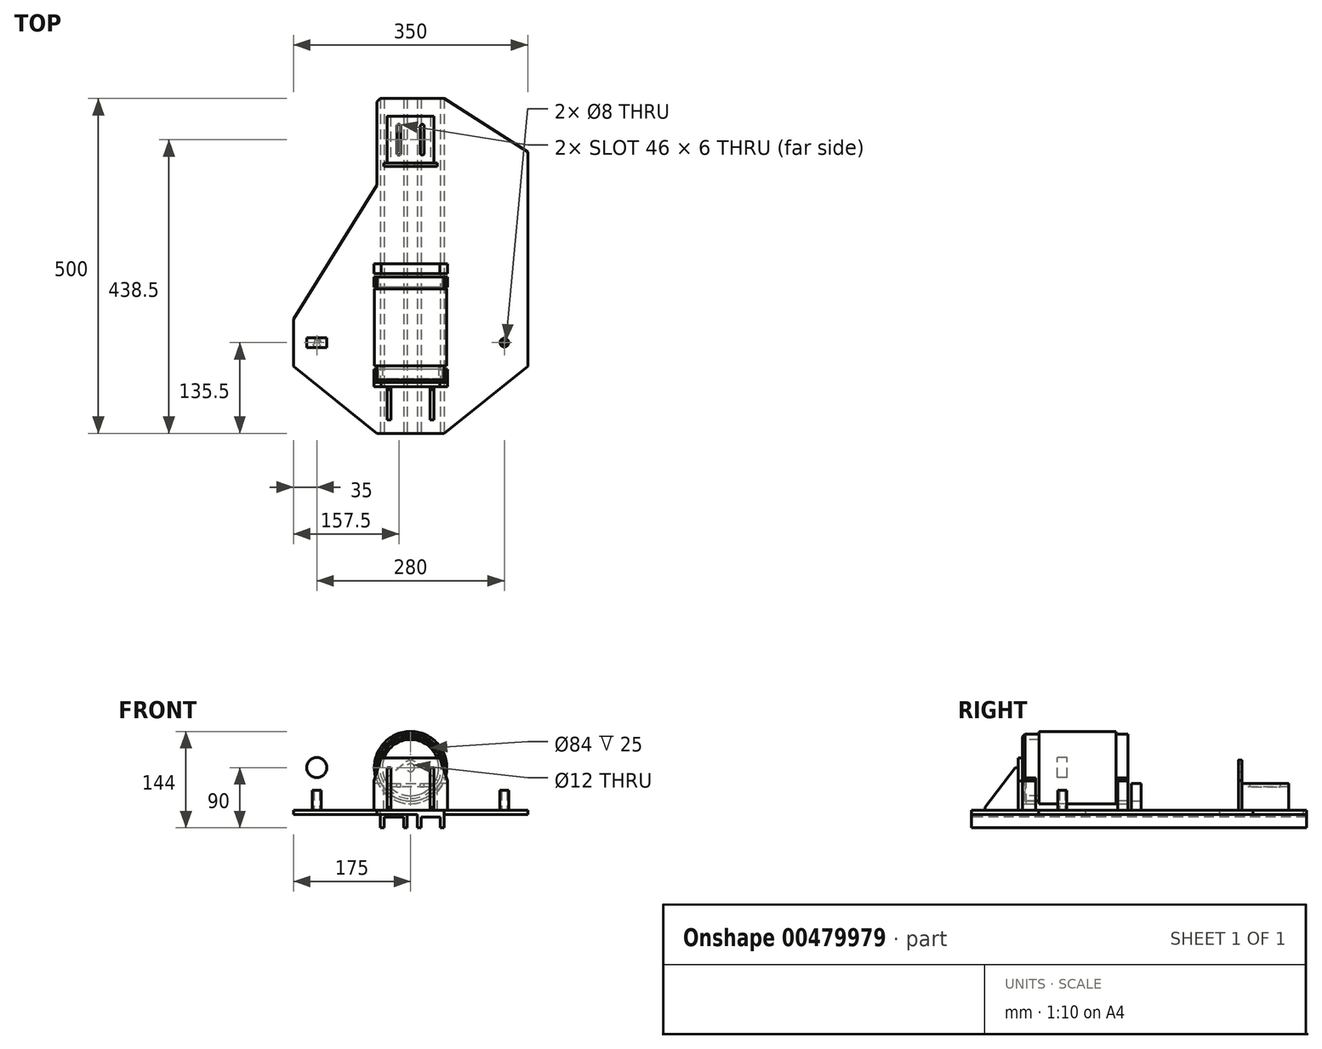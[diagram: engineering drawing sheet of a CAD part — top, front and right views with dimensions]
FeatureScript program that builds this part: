
annotation { "Feature Type Name" : "Feature", "Feature Type Description" : "" }
export const myFeature = defineFeature(function(context is Context, id is Id, definition is map)
    precondition{}
    {
        {
            var Q0;
            Q0=qCreatedBy(makeId("Front.planeOp"),FACE);
            var sketch = newSketch(context, id + "F0", { "sketchPlane" : qUnion([Q0])});
            skCircle(sketch, "E0", {"center": v(0, 0) * mm, "radius": 50 * mm});
            skSolve(sketch);
        }
        {
            var Q0;
            Q0=makeQuery(id+"F0.imprint","IMPRINT",FACE,{"disambiguationData":[TD([[makeQuery(id+"F0.imprint","IMPRINT",EDGE,{"derivedFrom":sQuery(id+"F0.wireOp",EDGE,"E0")}),1.0]])]});
            extrude(context, id + "F1", {"entities" : qUnion([Q0]), "oppositeDirection" : true, "depth" : 25 * mm});
        }
        {
            var Q0;
            Q0=makeQuery(id+"F1.opExtrude","CAP_FACE",FACE,{"disambiguationData":[OSD([sQuery(id+"F0.wireOp",EDGE,"E0")])],"isStart":false});
            var sketch = newSketch(context, id + "F2", { "sketchPlane" : qUnion([Q0])});
            skCircle(sketch, "E1", {"center": v(0, 0) * mm, "radius": 54 * mm});
            skSolve(sketch);
        }
        {
            var Q0;
            Q0=makeQuery(id+"F2.imprint","IMPRINT",FACE,{"disambiguationData":[TD([[makeQuery(id+"F2.imprint","IMPRINT",EDGE,{"derivedFrom":sQuery(id+"F2.wireOp",EDGE,"E1")}),1.0]])]});
            var Q1;
            Q1=makeQuery(id+"F2.imprint","IMPRINT",FACE,{"disambiguationData":[TD([[makeQuery(id+"F2.imprint","IMPRINT",EDGE,{"derivedFrom":makeQuery(id+"F1.opExtrude","CAP_EDGE",EDGE,{"disambiguationData":[OSD([sQuery(id+"F0.wireOp",EDGE,"E0")])],"isStart":false})}),-1.0]])]});
            extrude(context, id + "F3", {"entities" : qUnion([Q0, Q1]), "operationType" : NewBodyOperationType.ADD, "depth" : 115 * mm});
        }
        {
            var Q0;
            Q0=makeQuery(id+"F3.opExtrude","CAP_FACE",FACE,{"disambiguationData":[OSD([sQuery(id+"F2.wireOp",EDGE,"E1")])],"isStart":false});
            var sketch = newSketch(context, id + "F4", { "sketchPlane" : qUnion([Q0])});
            skCircle(sketch, "E2", {"center": v(0, 0) * mm, "radius": 50 * mm});
            skSolve(sketch);
        }
        {
            var Q0;
            Q0=makeQuery(id+"F4.imprint","IMPRINT",FACE,{"disambiguationData":[TD([[makeQuery(id+"F4.imprint","IMPRINT",EDGE,{"derivedFrom":sQuery(id+"F4.wireOp",EDGE,"E2")}),1.0]])]});
            extrude(context, id + "F5", {"entities" : qUnion([Q0]), "operationType" : NewBodyOperationType.ADD, "depth" : 17.5 * mm});
        }
        {
            var Q0;
            Q0=makeQuery(id+"F0.imprint","IMPRINT",FACE,{"disambiguationData":[TD([[makeQuery(id+"F0.imprint","IMPRINT",EDGE,{"derivedFrom":sQuery(id+"F0.wireOp",EDGE,"E0")}),1.0]])]});
            var sketch = newSketch(context, id + "F6", { "sketchPlane" : qUnion([Q0])});
            skCircle(sketch, "E3", {"center": v(0, 0) * mm, "radius": 42 * mm});
            skSolve(sketch);
        }
        {
            var Q0;
            Q0=makeQuery(id+"F6.imprint","IMPRINT",FACE,{"disambiguationData":[TD([[makeQuery(id+"F6.imprint","IMPRINT",EDGE,{"derivedFrom":sQuery(id+"F6.wireOp",EDGE,"E3")}),1.0]])]});
            var Q1;
            Q1=sQuery(id+"F6.wireOp",EDGE,"E3");
            extrude(context, id + "F7", {"entities" : qUnion([Q0]), "operationType" : NewBodyOperationType.REMOVE, "surfaceEntities" : qUnion([Q1]), "oppositeDirection" : true, "depth" : 25 * mm, "offsetDistance" : 25 * mm});
        }
        {
            var Q0;
            Q0=makeQuery(id+"F3.opExtrude","CAP_FACE",FACE,{"disambiguationData":[OSD([sQuery(id+"F2.wireOp",EDGE,"E1")])],"isStart":true});
            cPlane(context, id + "F8", {"entities" : qUnion([Q0]), "cplaneType" : CPlaneType.OFFSET, "offset" : 27 * mm, "oppositeDirection" : true, "width" : 150 * mm, "height" : 150 * mm});
        }
        {
            var Q0;
            Q0=qCreatedBy(id+"F8.planeOp",FACE);
            var sketch = newSketch(context, id + "F9", { "sketchPlane" : qUnion([Q0])});
            skLineSegment(sketch, "E4", {"start": v(0, 0) * mm, "end": v(-140, 0) * mm, "construction": true});
            skCircle(sketch, "E5", {"center": v(-140, 0) * mm, "radius": 13.5 * mm});
            skCircle(sketch, "E6", {"center": v(-140, 0) * mm, "radius": 15 * mm});
            skSolve(sketch);
        }
        {
            var Q0;
            Q0=makeQuery(id+"F9.imprint","IMPRINT",FACE,{"disambiguationData":[TD([[makeQuery(id+"F9.imprint","IMPRINT",EDGE,{"derivedFrom":sQuery(id+"F9.wireOp",EDGE,"E5")}),1.0]])]});
            var Q1;
            Q1=makeQuery(id+"F9.imprint","IMPRINT",FACE,{"disambiguationData":[TD([[makeQuery(id+"F9.imprint","IMPRINT",EDGE,{"derivedFrom":sQuery(id+"F9.wireOp",EDGE,"E5")}),-1.0]])]});
            extrude(context, id + "F10", {"entities" : qUnion([Q0, Q1]), "oppositeDirection" : true, "depth" : 15 * mm});
        }
        {
            var Q0;
            Q0=makeQuery(id+"F5.opExtrude","CAP_FACE",FACE,{"disambiguationData":[OSD([sQuery(id+"F4.wireOp",EDGE,"E2")])],"isStart":false});
            var sketch = newSketch(context, id + "F11", { "sketchPlane" : qUnion([Q0])});
            skCircle(sketch, "E7.0", {"center": v(0, 0) * mm, "radius": 50 * mm});
            skLineSegment(sketch, "E8", {"start": v(0, 0) * mm, "end": v(-48.3, -12.94) * mm, "construction": true});
            skLineSegment(sketch, "E9", {"start": v(0, 0) * mm, "end": v(-50, 0) * mm, "construction": true});
            skLineSegment(sketch, "E10", {"start": v(-55, -19.64) * mm, "end": v(-55, -64) * mm});
            skLineSegment(sketch, "E11", {"start": v(-55, -64) * mm, "end": v(0, -64) * mm});
            skCircle(sketch, "E12.0", {"center": v(0, 0) * mm, "radius": 54 * mm});
            skLineSegment(sketch, "E13", {"start": v(-52.4, -15.69) * mm, "end": v(-47.48, -15.69) * mm});
            skLineSegment(sketch, "E14", {"start": v(0, -64) * mm, "end": v(55, -64) * mm});
            skLineSegment(sketch, "E15", {"start": v(55, -64) * mm, "end": v(55, -19.64) * mm});
            skLineSegment(sketch, "E16", {"start": v(0, 0) * mm, "end": v(0, -64) * mm, "construction": true});
            skLineSegment(sketch, "E17", {"start": v(52.4, -15.69) * mm, "end": v(47.48, -15.69) * mm});
            skLineSegment(sketch, "E18", {"start": v(-55, -19.64) * mm, "end": v(-52.4, -15.69) * mm});
            skLineSegment(sketch, "E19", {"start": v(55, -19.64) * mm, "end": v(52.4, -15.69) * mm});
            skLineSegment(sketch, "E20", {"start": v(0, 0) * mm, "end": v(-38.18, -38.18) * mm, "construction": true});
            skLineSegment(sketch, "E21", {"start": v(-35.36, -35.36) * mm, "end": v(0, -35.36) * mm, "construction": true});
            skSolve(sketch);
        }
        {
            var Q0;
            {var subQ0=sQuery(id+"F11.wireOp",EDGE,"E13");var subQ1=sQuery(id+"F11.wireOp",EDGE,"E7.0");var subQ2=makeQuery(id+"F11.imprint","INTERSECT",VERTEX,{"derivedFrom":[subQ1,subQ0]});Q0=makeQuery(id+"F11.imprint","IMPRINT",FACE,{"disambiguationData":[TD([[makeQuery(id+"F11.imprint","IMPRINT",EDGE,{"disambiguationData":[TD([[subQ2,-1.0]])],"derivedFrom":subQ1}),-1.0]])]});}
            extrude(context, id + "F12", {"entities" : qUnion([Q0]), "oppositeDirection" : true, "depth" : 15 * mm});
        }
        {
            var Q0;
            Q0=makeQuery(id+"F11.imprint","IMPRINT",FACE,{"disambiguationData":[TD([[makeQuery(id+"F11.imprint","IMPRINT",EDGE,{"derivedFrom":sQuery(id+"F11.wireOp",EDGE,"E10")}),1.0]])]});
            extrude(context, id + "F13", {"entities" : qUnion([Q0]), "oppositeDirection" : true, "depth" : 15 * mm});
        }
        {
            var Q0;
            Q0=makeQuery(id+"F12.opExtrude","SWEPT_BODY",BODY,{"disambiguationData":[OSD([sQuery(id+"F11.wireOp",EDGE,"E7.0"),sQuery(id+"F11.wireOp",EDGE,"E12.0"),sQuery(id+"F11.wireOp",EDGE,"E13"),sQuery(id+"F11.wireOp",EDGE,"E17")])]});
            transform(context, id + "F14", {"entities" : qUnion([Q0]), "transformType" : TransformType.TRANSLATION_3D, "dx" : 0 * mm, "dy" : -137.5 * mm, "dz" : 0 * mm, "makeCopy" : true});
        }
        {
            var Q0;
            Q0=makeQuery(id+"F1.opExtrude","CAP_FACE",FACE,{"disambiguationData":[OSD([sQuery(id+"F0.wireOp",EDGE,"E0")])],"isStart":true});
            var sketch = newSketch(context, id + "F15", { "sketchPlane" : qUnion([Q0])});
            skLineSegment(sketch, "E22.0", {"start": v(-55, -64) * mm, "end": v(-55, -19.64) * mm});
            skLineSegment(sketch, "E23.0", {"start": v(-55, -19.64) * mm, "end": v(-52.4, -15.69) * mm});
            skLineSegment(sketch, "E24.0", {"start": v(-52.4, -15.69) * mm, "end": v(-47.48, -15.69) * mm});
            skLineSegment(sketch, "E25.0", {"start": v(52.4, -15.69) * mm, "end": v(47.48, -15.69) * mm});
            skLineSegment(sketch, "E26.0", {"start": v(55, -19.64) * mm, "end": v(52.4, -15.69) * mm});
            skLineSegment(sketch, "E27.0", {"start": v(55, -19.64) * mm, "end": v(55, -64) * mm});
            skLineSegment(sketch, "E28.0", {"start": v(55, -64) * mm, "end": v(0, -64) * mm});
            skLineSegment(sketch, "E28.1", {"start": v(0, -64) * mm, "end": v(-55, -64) * mm});
            skArc(sketch, "E29.0", {"start": v(51.67, -15.69) * mm, "mid": v(0, -54) * mm, "end": v(-51.67, -15.69) * mm});
            skLineSegment(sketch, "E30", {"start": v(-52.4, -15.69) * mm, "end": v(-30, 18.29) * mm});
            skLineSegment(sketch, "E31", {"start": v(-30, 18.29) * mm, "end": v(0, 18.29) * mm});
            skLineSegment(sketch, "E32", {"start": v(0, 18.29) * mm, "end": v(30, 18.29) * mm});
            skLineSegment(sketch, "E33", {"start": v(30, 18.29) * mm, "end": v(52.4, -15.69) * mm});
            skLineSegment(sketch, "E34", {"start": v(0, 18.29) * mm, "end": v(0, -64) * mm, "construction": true});
            skSolve(sketch);
        }
        {
            var Q0;
            Q0=makeQuery(id+"F3.opExtrude","CAP_FACE",FACE,{"disambiguationData":[OSD([sQuery(id+"F2.wireOp",EDGE,"E1")])],"isStart":true});
            var sketch = newSketch(context, id + "F16", { "sketchPlane" : qUnion([Q0])});
            skLineSegment(sketch, "E35.0", {"start": v(-55, -64) * mm, "end": v(-55, -19.64) * mm});
            skLineSegment(sketch, "E35.1", {"start": v(0, -64) * mm, "end": v(-55, -64) * mm});
            skLineSegment(sketch, "E35.2", {"start": v(55, -19.64) * mm, "end": v(55, -64) * mm});
            skLineSegment(sketch, "E35.3", {"start": v(55, -64) * mm, "end": v(0, -64) * mm});
            skLineSegment(sketch, "E35.4", {"start": v(55, -19.64) * mm, "end": v(52.4, -15.69) * mm});
            skLineSegment(sketch, "E35.5", {"start": v(30, 18.29) * mm, "end": v(55, -19.64) * mm});
            skLineSegment(sketch, "E35.6", {"start": v(-55, -19.64) * mm, "end": v(-52.4, -15.69) * mm});
            skLineSegment(sketch, "E35.7", {"start": v(-55, -19.64) * mm, "end": v(-30, 18.29) * mm});
            skArc(sketch, "E36.0", {"start": v(51.67, -15.69) * mm, "mid": v(0, -54) * mm, "end": v(-51.67, -15.69) * mm});
            skLineSegment(sketch, "E37", {"start": v(-51.67, -15.69) * mm, "end": v(-52.4, -15.69) * mm});
            skLineSegment(sketch, "E38", {"start": v(51.67, -15.69) * mm, "end": v(52.4, -15.69) * mm});
            skSolve(sketch);
        }
        {
            var Q0;
            {var subQ2=sQuery(id+"F16.wireOp",EDGE,"E35.0");Q0=makeQuery(id+"F16.imprint","IMPRINT",FACE,{"disambiguationData":[TD([[makeQuery(id+"F16.imprint","IMPRINT",EDGE,{"derivedFrom":subQ2}),-1.0]])]});}
            extrude(context, id + "F17", {"entities" : qUnion([Q0]), "depth" : 25 * mm, "hasSecondDirection" : true, "secondDirectionOppositeDirection" : false, "secondDirectionDepth" : 5 * mm, "offsetDistance" : 25 * mm});
        }
        {
            var Q0;
            Q0=qCreatedBy(makeId("Right.planeOp"),FACE);
            cPlane(context, id + "F18", {"entities" : qUnion([Q0]), "cplaneType" : CPlaneType.OFFSET, "offset" : 35 * mm, "width" : 150 * mm, "height" : 150 * mm});
        }
        {
            var Q0;
            Q0=qCreatedBy(id+"F18.planeOp",FACE);
            var sketch = newSketch(context, id + "F19", { "sketchPlane" : qUnion([Q0])});
            skLineSegment(sketch, "E39.0", {"start": v(-6, 18.29) * mm, "end": v(-6, -19.64) * mm});
            skLineSegment(sketch, "E40.0", {"start": v(-6, -19.64) * mm, "end": v(-6, -64) * mm});
            skLineSegment(sketch, "E41", {"start": v(-6, -64) * mm, "end": v(-56, -64) * mm});
            skLineSegment(sketch, "E42", {"start": v(-56, -64) * mm, "end": v(-56, -59) * mm});
            skLineSegment(sketch, "E43", {"start": v(-56, -59) * mm, "end": v(-11, 0) * mm});
            skLineSegment(sketch, "E44", {"start": v(-11, 0) * mm, "end": v(-6, 0) * mm});
            skSolve(sketch);
        }
        {
            var Q0;
            {var subQ0=sQuery(id+"F19.wireOp",EDGE,"E40.0");Q0=makeQuery(id+"F19.imprint","IMPRINT",FACE,{"disambiguationData":[TD([[makeQuery(id+"F19.imprint","IMPRINT",EDGE,{"derivedFrom":subQ0}),-1.0]])]});}
            extrude(context, id + "F20", {"entities" : qUnion([Q0]), "oppositeDirection" : true, "depth" : 6 * mm});
        }
        {
            var Q0;
            Q0=makeQuery(id+"F20.opExtrude","SWEPT_BODY",BODY,{"disambiguationData":[OSD([sQuery(id+"F19.wireOp",EDGE,"E39.0"),sQuery(id+"F19.wireOp",EDGE,"E40.0"),sQuery(id+"F19.wireOp",EDGE,"E41"),sQuery(id+"F19.wireOp",EDGE,"E42"),sQuery(id+"F19.wireOp",EDGE,"E43"),sQuery(id+"F19.wireOp",EDGE,"E44")])]});
            transform(context, id + "F21", {"entities" : qUnion([Q0]), "transformType" : TransformType.TRANSLATION_3D, "dx" : -64 * mm, "dy" : 0 * mm, "dz" : 0 * mm, "makeCopy" : true});
        }
        {
            var Q0;
            {var subQ0=sQuery(id+"F11.wireOp",EDGE,"E7.0");var subQ1=makeQuery(id+"F11.imprint","INTERSECT",VERTEX,{"derivedFrom":[subQ0,sQuery(id+"F11.wireOp",EDGE,"E13")]});Q0=makeQuery(id+"F11.imprint","IMPRINT",FACE,{"disambiguationData":[TD([[makeQuery(id+"F11.imprint","IMPRINT",EDGE,{"disambiguationData":[TD([[subQ1,-1.0]])],"derivedFrom":subQ0}),1.0]])]});}
            cPlane(context, id + "F22", {"entities" : qUnion([Q0]), "cplaneType" : CPlaneType.OFFSET, "offset" : 25 * mm, "width" : 150 * mm, "height" : 150 * mm});
        }
        {
            var Q0;
            Q0=qCreatedBy(id+"F22.planeOp",FACE);
            var sketch = newSketch(context, id + "F23", { "sketchPlane" : qUnion([Q0])});
            skCircle(sketch, "E45.0", {"center": v(0, 0) * mm, "radius": 50 * mm});
            skLineSegment(sketch, "E46.0", {"start": v(0, -64) * mm, "end": v(55, -64) * mm});
            skLineSegment(sketch, "E46.1", {"start": v(-55, -64) * mm, "end": v(0, -64) * mm});
            skLineSegment(sketch, "E46.3", {"start": v(-55, -19.64) * mm, "end": v(-55, -64) * mm});
            skLineSegment(sketch, "E47", {"start": v(-55, -24) * mm, "end": v(-43.86, -24) * mm});
            skLineSegment(sketch, "E48", {"start": v(55, -64) * mm, "end": v(55, -19.64) * mm});
            skLineSegment(sketch, "E49", {"start": v(43.86, -24) * mm, "end": v(55, -24) * mm});
            skLineSegment(sketch, "E50", {"start": v(0, -64) * mm, "end": v(0, -22.33) * mm, "construction": true});
            skSolve(sketch);
        }
        {
            var Q0;
            Q0=makeQuery(id+"F23.imprint","IMPRINT",FACE,{"disambiguationData":[TD([[makeQuery(id+"F23.imprint","IMPRINT",EDGE,{"derivedFrom":sQuery(id+"F23.wireOp",EDGE,"E46.0")}),1.0]])]});
            extrude(context, id + "F24", {"entities" : qUnion([Q0]), "oppositeDirection" : true, "depth" : 20 * mm});
        }
        {
            var Q0;
            Q0=makeQuery(id+"F17.opExtrude","SWEPT_FACE",FACE,{"disambiguationData":[OSD([sQuery(id+"F16.wireOp",EDGE,"E35.1"),sQuery(id+"F16.wireOp",EDGE,"E35.3")])]});
            var sketch = newSketch(context, id + "F25", { "sketchPlane" : qUnion([Q0])});
            skLineSegment(sketch, "E51", {"start": v(-175, -24) * mm, "end": v(-175, -95) * mm});
            skLineSegment(sketch, "E52", {"start": v(-175, -95) * mm, "end": v(-50, -295) * mm});
            skLineSegment(sketch, "E53", {"start": v(-50, -295) * mm, "end": v(-50, -424) * mm});
            skLineSegment(sketch, "E54", {"start": v(-50, -424) * mm, "end": v(50, -424) * mm});
            skLineSegment(sketch, "E55", {"start": v(50, -424) * mm, "end": v(50, -295) * mm});
            skLineSegment(sketch, "E56", {"start": v(50, -295) * mm, "end": v(175, -95) * mm});
            skLineSegment(sketch, "E57", {"start": v(175, -95) * mm, "end": v(175, -24) * mm});
            skLineSegment(sketch, "E58", {"start": v(175, -24) * mm, "end": v(50, 76) * mm});
            skLineSegment(sketch, "E59", {"start": v(50, 76) * mm, "end": v(-50, 76) * mm});
            skLineSegment(sketch, "E60", {"start": v(-50, 76) * mm, "end": v(-175, -24) * mm});
            skLineSegment(sketch, "E61", {"start": v(0, 0) * mm, "end": v(0, -424) * mm, "construction": true});
            skLineSegment(sketch, "E62", {"start": v(-175, -59.5) * mm, "end": v(175, -59.5) * mm, "construction": true});
            skLineSegment(sketch, "E63.0", {"start": v(-155, -52) * mm, "end": v(-125, -52) * mm, "construction": true});
            skLineSegment(sketch, "E63.1", {"start": v(-155, -67) * mm, "end": v(-125, -67) * mm, "construction": true});
            skLineSegment(sketch, "E64", {"start": v(-155, -52) * mm, "end": v(-155, -67) * mm, "construction": true});
            skLineSegment(sketch, "E65", {"start": v(-155, -59.5) * mm, "end": v(-171.28, -59.5) * mm, "construction": true});
            skSolve(sketch);
        }
        {
            var Q0;
            Q0=makeQuery(id+"F25.imprint","IMPRINT",FACE,{"disambiguationData":[TD([[makeQuery(id+"F25.imprint","IMPRINT",EDGE,{"derivedFrom":sQuery(id+"F25.wireOp",EDGE,"E51")}),1.0]])]});
            var Q1;
            {var subQ0=sQuery(id+"F16.wireOp",EDGE,"E35.1");Q1=makeQuery(id+"F25.imprint","IMPRINT",FACE,{"disambiguationData":[TD([[makeQuery(id+"F25.imprint","IMPRINT",EDGE,{"derivedFrom":makeQuery(id+"F17.opExtrude","SWEPT_EDGE",EDGE,{"disambiguationData":[OSD([sQuery(id+"F16.wireOp",EDGE,"E35.0"),subQ0])]})}),1.0]])]});}
            extrude(context, id + "F26", {"entities" : qUnion([Q0, Q1]), "depth" : 6 * mm});
        }
        {
            var Q0;
            Q0=makeQuery(id+"F10.opExtrude","CAP_FACE",FACE,{"disambiguationData":[OSD([sQuery(id+"F9.wireOp",EDGE,"E6")])],"isStart":false});
            cPlane(context, id + "F27", {"entities" : qUnion([Q0]), "cplaneType" : CPlaneType.OFFSET, "offset" : 7.5 * mm, "oppositeDirection" : true, "width" : 150 * mm, "height" : 150 * mm});
        }
        {
            var Q0;
            Q0=qCreatedBy(id+"F27.planeOp",FACE);
            var sketch = newSketch(context, id + "F28", { "sketchPlane" : qUnion([Q0])});
            skCircle(sketch, "E66.0", {"center": v(140, 0) * mm, "radius": 15 * mm, "construction": true});
            skLineSegment(sketch, "E67.0", {"start": v(175, -64) * mm, "end": v(50, -64) * mm});
            skLineSegment(sketch, "E68", {"start": v(140, 0) * mm, "end": v(140, -64) * mm, "construction": true});
            skLineSegment(sketch, "E69", {"start": v(0, 0) * mm, "end": v(0, -100) * mm, "construction": true});
            skSolve(sketch);
        }
        {
            var Q0;
            Q0=makeQuery(id+"F1.opExtrude","CAP_EDGE",EDGE,{"disambiguationData":[OSD([sQuery(id+"F0.wireOp",EDGE,"E0")])],"isStart":true});
            chamfer(context, id + "F29", {"entities" : qUnion([Q0]), "width" : 4 * mm, "tangentPropagation" : true});
        }
        {
            var Q0;
            Q0=makeQuery(id+"F24.opExtrude","CAP_FACE",FACE,{"disambiguationData":[OSD([sQuery(id+"F23.wireOp",EDGE,"E45.0"),sQuery(id+"F23.wireOp",EDGE,"E46.0"),sQuery(id+"F23.wireOp",EDGE,"E46.1"),sQuery(id+"F23.wireOp",EDGE,"E46.2"),sQuery(id+"F23.wireOp",EDGE,"E46.3"),sQuery(id+"F23.wireOp",EDGE,"E47"),sQuery(id+"F23.wireOp",EDGE,"y394r1G8-uPi8-XqdF-46gs-KCEQsSj5C9bU")])],"isStart":true});
            cPlane(context, id + "F30", {"entities" : qUnion([Q0]), "cplaneType" : CPlaneType.OFFSET, "offset" : 145 * mm, "width" : 150 * mm, "height" : 150 * mm});
        }
        {
            var Q0;
            Q0=qCreatedBy(id+"F30.planeOp",FACE);
            var sketch = newSketch(context, id + "F31", { "sketchPlane" : qUnion([Q0])});
            skLineSegment(sketch, "E70.0", {"start": v(-55, -64) * mm, "end": v(55, -64) * mm, "construction": true});
            skLineSegment(sketch, "E71", {"start": v(0, -64) * mm, "end": v(0, 0) * mm, "construction": true});
            skLineSegment(sketch, "E72", {"start": v(-35, -64) * mm, "end": v(-30, -64) * mm});
            skLineSegment(sketch, "E73", {"start": v(-30, -64) * mm, "end": v(-30, -29) * mm});
            skLineSegment(sketch, "E74", {"start": v(-30, -29) * mm, "end": v(30, -29) * mm});
            skLineSegment(sketch, "E75", {"start": v(30, -29) * mm, "end": v(30, -64) * mm});
            skLineSegment(sketch, "E76", {"start": v(30, -64) * mm, "end": v(35, -64) * mm});
            skLineSegment(sketch, "E77", {"start": v(35, -64) * mm, "end": v(35, -24) * mm});
            skLineSegment(sketch, "E78", {"start": v(35, -24) * mm, "end": v(-35, -24) * mm});
            skLineSegment(sketch, "E79", {"start": v(-35, -24) * mm, "end": v(-35, -64) * mm});
            skSolve(sketch);
        }
        {
            var Q0;
            Q0=makeQuery(id+"F31.imprint","IMPRINT",FACE,{"disambiguationData":[TD([[makeQuery(id+"F31.imprint","IMPRINT",EDGE,{"derivedFrom":sQuery(id+"F31.wireOp",EDGE,"E72")}),1.0]])]});
            extrude(context, id + "F32", {"entities" : qUnion([Q0]), "depth" : 70 * mm});
        }
        {
            var Q0;
            Q0=makeQuery(id+"F32.opExtrude","SWEPT_EDGE",EDGE,{"disambiguationData":[OSD([sQuery(id+"F31.wireOp",EDGE,"E78"),sQuery(id+"F31.wireOp",EDGE,"E79")])]});
            var Q1;
            Q1=makeQuery(id+"F32.opExtrude","SWEPT_EDGE",EDGE,{"disambiguationData":[OSD([sQuery(id+"F31.wireOp",EDGE,"E77"),sQuery(id+"F31.wireOp",EDGE,"E78")])]});
            var Q2;
            Q2=makeQuery(id+"F32.opExtrude","SWEPT_EDGE",EDGE,{"disambiguationData":[OSD([sQuery(id+"F31.wireOp",EDGE,"E74"),sQuery(id+"F31.wireOp",EDGE,"E75")])]});
            var Q3;
            Q3=makeQuery(id+"F32.opExtrude","SWEPT_EDGE",EDGE,{"disambiguationData":[OSD([sQuery(id+"F31.wireOp",EDGE,"E73"),sQuery(id+"F31.wireOp",EDGE,"E74")])]});
            fillet(context, id + "F33", {"entities" : qUnion([Q0, Q1, Q2, Q3]), "radius" : 5 * mm, "tangentPropagation" : true, "allowEdgeOverflow" : false});
        }
        {
            var Q0;
            Q0=makeQuery(id+"F32.opExtrude","SWEPT_FACE",FACE,{"disambiguationData":[OSD([sQuery(id+"F31.wireOp",EDGE,"E78")])]});
            var sketch = newSketch(context, id + "F34", { "sketchPlane" : qUnion([Q0])});
            skLineSegment(sketch, "E80", {"start": v(0, 327.5) * mm, "end": v(0, 397.5) * mm, "construction": true});
            skLineSegment(sketch, "E81", {"start": v(-17.5, 327.5) * mm, "end": v(-17.5, 397.5) * mm, "construction": true});
            skLineSegment(sketch, "E82", {"start": v(17.5, 327.5) * mm, "end": v(17.5, 397.5) * mm, "construction": true});
            skLineSegment(sketch, "E83.bottom", {"start": v(-20.5, 342.5) * mm, "end": v(-14.5, 342.5) * mm, "construction": true});
            skLineSegment(sketch, "E83.top", {"start": v(-20.5, 382.5) * mm, "end": v(-14.5, 382.5) * mm, "construction": true});
            skLineSegment(sketch, "E83.left", {"start": v(-20.5, 342.5) * mm, "end": v(-20.5, 382.5) * mm});
            skLineSegment(sketch, "E83.right", {"start": v(-14.5, 342.5) * mm, "end": v(-14.5, 382.5) * mm});
            skArc(sketch, "E84", {"start": v(-20.5, 342.5) * mm, "mid": v(-17.5, 339.5) * mm, "end": v(-14.5, 342.5) * mm});
            skArc(sketch, "E85", {"start": v(-14.5, 382.5) * mm, "mid": v(-17.5, 385.5) * mm, "end": v(-20.5, 382.5) * mm});
            skLineSegment(sketch, "E86", {"start": v(-17.5, 362.5) * mm, "end": v(17.5, 362.5) * mm, "construction": true});
            skLineSegment(sketch, "E87.bottom", {"start": v(14.5, 342.5) * mm, "end": v(20.5, 342.5) * mm, "construction": true});
            skLineSegment(sketch, "E87.top", {"start": v(14.5, 382.5) * mm, "end": v(20.5, 382.5) * mm, "construction": true});
            skLineSegment(sketch, "E87.left", {"start": v(14.5, 342.5) * mm, "end": v(14.5, 382.5) * mm});
            skLineSegment(sketch, "E87.right", {"start": v(20.5, 342.5) * mm, "end": v(20.5, 382.5) * mm});
            skArc(sketch, "E88", {"start": v(14.5, 342.5) * mm, "mid": v(17.5, 339.5) * mm, "end": v(20.5, 342.5) * mm});
            skArc(sketch, "E89", {"start": v(20.5, 382.5) * mm, "mid": v(17.5, 385.5) * mm, "end": v(14.5, 382.5) * mm});
            skSolve(sketch);
        }
        {
            var Q0;
            Q0=makeQuery(id+"F34.imprint","IMPRINT",FACE,{"disambiguationData":[TD([[makeQuery(id+"F34.imprint","IMPRINT",EDGE,{"derivedFrom":sQuery(id+"F34.wireOp",EDGE,"E83.left")}),-1.0]])]});
            var Q1;
            Q1=makeQuery(id+"F34.imprint","IMPRINT",FACE,{"disambiguationData":[TD([[makeQuery(id+"F34.imprint","IMPRINT",EDGE,{"derivedFrom":sQuery(id+"F34.wireOp",EDGE,"E87.left")}),-1.0]])]});
            extrude(context, id + "F35", {"entities" : qUnion([Q0, Q1]), "operationType" : NewBodyOperationType.REMOVE, "oppositeDirection" : true, "depth" : 25 * mm, "hasSecondDirection" : true, "secondDirectionOppositeDirection" : false, "secondDirectionDepth" : 25 * mm});
        }
        {
            var Q0;
            Q0=makeQuery(id+"F26.opExtrude","SWEPT_EDGE",EDGE,{"disambiguationData":[OSD([sQuery(id+"F25.wireOp",EDGE,"E54"),sQuery(id+"F25.wireOp",EDGE,"E55")])]});
            var Q1;
            Q1=makeQuery(id+"F26.opExtrude","SWEPT_EDGE",EDGE,{"disambiguationData":[OSD([sQuery(id+"F25.wireOp",EDGE,"E53"),sQuery(id+"F25.wireOp",EDGE,"E54")])]});
            chamfer(context, id + "F36", {"entities" : qUnion([Q0, Q1]), "width" : 5 * mm, "tangentPropagation" : true});
        }
        {
            var Q0;
            Q0=makeQuery(id+"F26.opExtrude","CAP_FACE",FACE,{"disambiguationData":[OSD([sQuery(id+"F25.wireOp",EDGE,"E51"),sQuery(id+"F25.wireOp",EDGE,"E52"),sQuery(id+"F25.wireOp",EDGE,"E53"),sQuery(id+"F25.wireOp",EDGE,"E54"),sQuery(id+"F25.wireOp",EDGE,"E55"),sQuery(id+"F25.wireOp",EDGE,"E56"),sQuery(id+"F25.wireOp",EDGE,"E57"),sQuery(id+"F25.wireOp",EDGE,"E58"),sQuery(id+"F25.wireOp",EDGE,"E59"),sQuery(id+"F25.wireOp",EDGE,"E60")])],"isStart":true});
            var sketch = newSketch(context, id + "F37", { "sketchPlane" : qUnion([Q0])});
            skLineSegment(sketch, "E90.0", {"start": v(-125, 52) * mm, "end": v(-155, 52) * mm, "construction": true});
            skLineSegment(sketch, "E91.0", {"start": v(-125, 67) * mm, "end": v(-155, 67) * mm, "construction": true});
            skLineSegment(sketch, "E92", {"start": v(-155, 67) * mm, "end": v(-155, 52) * mm, "construction": true});
            skLineSegment(sketch, "E93", {"start": v(-125, 67) * mm, "end": v(-125, 52) * mm, "construction": true});
            skLineSegment(sketch, "E94", {"start": v(-155, 59.5) * mm, "end": v(-125, 59.5) * mm, "construction": true});
            skCircle(sketch, "E95", {"center": v(-140, 59.5) * mm, "radius": 6.5 * mm});
            skCircle(sketch, "E96", {"center": v(-140, 59.5) * mm, "radius": 4 * mm});
            skSolve(sketch);
        }
        {
            var Q0;
            Q0 = qSketchRegion(id + "F37", true);
            extrude(context, id + "F38", {"entities" : qUnion([Q0]), "depth" : 30 * mm});
        }
        {
            var Q0;
            Q0=makeQuery(id+"F38.opExtrude","SWEPT_BODY",BODY,{"disambiguationData":[OSD([sQuery(id+"F37.wireOp",EDGE,"E95"),sQuery(id+"F37.wireOp",EDGE,"E96")])]});
            var Q1;
            Q1=sQuery(id+"F28.wireOp",EDGE,"E69");
            transform(context, id + "F39", {"entities" : qUnion([Q0]), "transformType" : TransformType.ROTATION, "transformAxis" : qUnion([Q1]), "angle" : 180 * degree, "makeCopy" : true});
        }
        {
            var Q0;
            Q0=makeQuery(id+"F26.opExtrude","CAP_FACE",FACE,{"disambiguationData":[OSD([sQuery(id+"F25.wireOp",EDGE,"E51"),sQuery(id+"F25.wireOp",EDGE,"E52"),sQuery(id+"F25.wireOp",EDGE,"E53"),sQuery(id+"F25.wireOp",EDGE,"E54"),sQuery(id+"F25.wireOp",EDGE,"E55"),sQuery(id+"F25.wireOp",EDGE,"E56"),sQuery(id+"F25.wireOp",EDGE,"E57"),sQuery(id+"F25.wireOp",EDGE,"E58"),sQuery(id+"F25.wireOp",EDGE,"E59"),sQuery(id+"F25.wireOp",EDGE,"E60")])],"isStart":false});
            var sketch = newSketch(context, id + "F40", { "sketchPlane" : qUnion([Q0])});
            skLineSegment(sketch, "E97", {"start": v(35, -424) * mm, "end": v(35, 76) * mm});
            skLineSegment(sketch, "E98", {"start": v(0, 76) * mm, "end": v(0, -424) * mm, "construction": true});
            skLineSegment(sketch, "E99.0", {"start": v(50, 76) * mm, "end": v(-50, 76) * mm});
            skLineSegment(sketch, "E100.0", {"start": v(-45, -424) * mm, "end": v(45, -424) * mm});
            skLineSegment(sketch, "E101", {"start": v(15, 76) * mm, "end": v(15, -424) * mm});
            skLineSegment(sketch, "E102", {"start": v(-15, 76) * mm, "end": v(-15, -424) * mm});
            skLineSegment(sketch, "E103", {"start": v(-35, 76) * mm, "end": v(-35, -424) * mm});
            skSolve(sketch);
        }
        {
            var Q0;
            Q0=qCreatedBy(id+"F30.planeOp",FACE);
            var sketch = newSketch(context, id + "F41", { "sketchPlane" : qUnion([Q0])});
            skLineSegment(sketch, "E104.0", {"start": v(30, -64) * mm, "end": v(35, -64) * mm, "construction": true});
            skLineSegment(sketch, "E105.0", {"start": v(-35, -64) * mm, "end": v(-30, -64) * mm, "construction": true});
            skLineSegment(sketch, "E106", {"start": v(40, -64) * mm, "end": v(-40, -64) * mm});
            skCircle(sketch, "E107", {"center": v(0, 0) * mm, "radius": 6 * mm});
            skLineSegment(sketch, "E108", {"start": v(40, -64) * mm, "end": v(40, -19) * mm});
            skLineSegment(sketch, "E109", {"start": v(40, -19) * mm, "end": v(7.04, 8.45) * mm});
            skLineSegment(sketch, "E110", {"start": v(-40, -64) * mm, "end": v(-40, -19) * mm});
            skLineSegment(sketch, "E111", {"start": v(-40, -19) * mm, "end": v(-7.04, 8.45) * mm});
            skArc(sketch, "E112", {"start": v(7.04, 8.45) * mm, "mid": v(0, 11) * mm, "end": v(-7.04, 8.45) * mm});
            skLineSegment(sketch, "E113", {"start": v(0, 0) * mm, "end": v(0, -64) * mm, "construction": true});
            skSolve(sketch);
        }
        {
            var Q0;
            Q0=makeQuery(id+"F41.imprint","IMPRINT",FACE,{"disambiguationData":[TD([[makeQuery(id+"F41.imprint","IMPRINT",EDGE,{"derivedFrom":sQuery(id+"F41.wireOp",EDGE,"E106")}),-1.0]])]});
            extrude(context, id + "F42", {"entities" : qUnion([Q0]), "oppositeDirection" : true, "depth" : 5 * mm});
        }
        {
            var Q0;
            Q0=makeQuery(id+"F26.opExtrude","SWEPT_FACE",FACE,{"disambiguationData":[OSD([sQuery(id+"F25.wireOp",EDGE,"E59")])]});
            var sketch = newSketch(context, id + "F43", { "sketchPlane" : qUnion([Q0])});
            skLineSegment(sketch, "E114.0", {"start": v(0, 0) * mm, "end": v(0, -64) * mm, "construction": true});
            skLineSegment(sketch, "E115", {"start": v(50, -70) * mm, "end": v(50, -90) * mm});
            skLineSegment(sketch, "E116", {"start": v(50, -90) * mm, "end": v(44.5, -90) * mm});
            skLineSegment(sketch, "E117", {"start": v(44.5, -90) * mm, "end": v(44.5, -74) * mm});
            skLineSegment(sketch, "E118", {"start": v(44.5, -74) * mm, "end": v(15.5, -74) * mm});
            skLineSegment(sketch, "E119", {"start": v(15.5, -74) * mm, "end": v(15.5, -90) * mm});
            skLineSegment(sketch, "E120", {"start": v(15.5, -90) * mm, "end": v(10, -90) * mm});
            skLineSegment(sketch, "E121", {"start": v(10, -90) * mm, "end": v(10, -70) * mm});
            skLineSegment(sketch, "E122", {"start": v(10, -70) * mm, "end": v(50, -70) * mm});
            skLineSegment(sketch, "E123", {"start": v(30, -74) * mm, "end": v(30, -90) * mm, "construction": true});
            skLineSegment(sketch, "E124.0", {"start": v(50, -70) * mm, "end": v(50, -64) * mm, "construction": true});
            skSolve(sketch);
        }
        {
            var Q0;
            Q0=makeQuery(id+"F43.imprint","IMPRINT",FACE,{"disambiguationData":[TD([[makeQuery(id+"F43.imprint","IMPRINT",EDGE,{"derivedFrom":sQuery(id+"F43.wireOp",EDGE,"E115")}),-1.0]])]});
            var Q1;
            Q1=makeQuery(id+"F26.opExtrude","SWEPT_FACE",FACE,{"disambiguationData":[OSD([sQuery(id+"F25.wireOp",EDGE,"E54")])]});
            extrude(context, id + "F44", {"entities" : qUnion([Q0]), "endBound" : BoundingType.UP_TO_SURFACE, "oppositeDirection" : true, "depth" : 25 * mm, "endBoundEntityFace" : qUnion([Q1]), "offsetDistance" : 25 * mm});
        }
        {
            var Q0;
            Q0=makeQuery(id+"F44.opExtrude","SWEPT_BODY",BODY,{"disambiguationData":[OSD([sQuery(id+"F43.wireOp",EDGE,"E115"),sQuery(id+"F43.wireOp",EDGE,"E116"),sQuery(id+"F43.wireOp",EDGE,"E117"),sQuery(id+"F43.wireOp",EDGE,"E118"),sQuery(id+"F43.wireOp",EDGE,"E119"),sQuery(id+"F43.wireOp",EDGE,"E120"),sQuery(id+"F43.wireOp",EDGE,"E121"),sQuery(id+"F43.wireOp",EDGE,"E122")])]});
            var Q1;
            Q1=makeQuery(id+"F44.opExtrude","CAP_VERTEX",VERTEX,{"disambiguationData":[OSD([sQuery(id+"F25.wireOp",EDGE,"E59"),sQuery(id+"F43.wireOp",EDGE,"E121"),sQuery(id+"F43.wireOp",EDGE,"E122")])],"isStart":true});
            var Q2;
            Q2=sQuery(id+"F40.wireOp",VERTEX,"E99.0.end");
            transform(context, id + "F45", {"entities" : qUnion([Q0]), "transformType" : TransformType.TRANSLATION_ENTITY, "oppositeDirectionEntity" : false, "transformLine" : qUnion([Q1, Q2]), "makeCopy" : true});
        }
        {
            var Q0;
            Q0=makeQuery(id+"F0.imprint","IMPRINT",FACE,{"disambiguationData":[TD([[makeQuery(id+"F0.imprint","IMPRINT",EDGE,{"derivedFrom":sQuery(id+"F0.wireOp",EDGE,"E0")}),1.0]])]});
            var sketch = newSketch(context, id + "F46", { "sketchPlane" : qUnion([Q0])});
            skCircle(sketch, "E125.0", {"center": v(0, 0) * mm, "radius": 46 * mm, "construction": true});
            skCircle(sketch, "E126.0", {"center": v(0, 0) * mm, "radius": 42 * mm, "construction": true});
            skLineSegment(sketch, "E127.0", {"start": v(-55, -64) * mm, "end": v(-55, -19.64) * mm});
            skLineSegment(sketch, "E127.1", {"start": v(55, -19.64) * mm, "end": v(55, -64) * mm});
            skLineSegment(sketch, "E128", {"start": v(-55, -19.64) * mm, "end": v(-43.65, 14.5) * mm});
            skLineSegment(sketch, "E129", {"start": v(-43.65, 14.5) * mm, "end": v(43.65, 14.5) * mm});
            skLineSegment(sketch, "E130", {"start": v(43.65, 14.5) * mm, "end": v(55, -19.64) * mm});
            skLineSegment(sketch, "E131", {"start": v(-55, -64) * mm, "end": v(55, -64) * mm});
            skSolve(sketch);
        }
        {
            var Q0;
            {var subQ1=sQuery(id+"F46.wireOp",EDGE,"E127.0");Q0=makeQuery(id+"F46.imprint","IMPRINT",FACE,{"disambiguationData":[TD([[makeQuery(id+"F46.imprint","IMPRINT",EDGE,{"derivedFrom":subQ1}),-1.0]])]});}
            var Q1;
            {var subQ0=sQuery(id+"F46.wireOp",EDGE,"E129");Q1=makeQuery(id+"F46.imprint","IMPRINT",FACE,{"disambiguationData":[TD([[makeQuery(id+"F46.imprint","IMPRINT",EDGE,{"derivedFrom":subQ0}),-1.0]])]});}
            extrude(context, id + "F47", {"entities" : qUnion([Q0, Q1]), "depth" : 6 * mm, "offsetDistance" : 25 * mm});
        }
        {
            var Q0;
            Q0=makeQuery(id+"F26.opExtrude","CAP_FACE",FACE,{"disambiguationData":[OSD([sQuery(id+"F25.wireOp",EDGE,"E51"),sQuery(id+"F25.wireOp",EDGE,"E52"),sQuery(id+"F25.wireOp",EDGE,"E53"),sQuery(id+"F25.wireOp",EDGE,"E54"),sQuery(id+"F25.wireOp",EDGE,"E55"),sQuery(id+"F25.wireOp",EDGE,"E56"),sQuery(id+"F25.wireOp",EDGE,"E57"),sQuery(id+"F25.wireOp",EDGE,"E58"),sQuery(id+"F25.wireOp",EDGE,"E59"),sQuery(id+"F25.wireOp",EDGE,"E60")])],"isStart":false});
            var sketch = newSketch(context, id + "F48", { "sketchPlane" : qUnion([Q0])});
            skLineSegment(sketch, "E132", {"start": v(175, -95) * mm, "end": v(175, -344) * mm});
            skLineSegment(sketch, "E133.0", {"start": v(175, -95) * mm, "end": v(175, -24) * mm, "construction": true});
            skLineSegment(sketch, "E134.0", {"start": v(50, -424) * mm, "end": v(50, 76) * mm, "construction": true});
            skLineSegment(sketch, "E135", {"start": v(175, -344) * mm, "end": v(50, -424) * mm});
            skLineSegment(sketch, "E136", {"start": v(50, -424) * mm, "end": v(45, -424) * mm});
            skSolve(sketch);
        }
        {
            var Q0;
            Q0=makeQuery(id+"F48.imprint","IMPRINT",FACE,{"disambiguationData":[TD([[makeQuery(id+"F48.imprint","IMPRINT",EDGE,{"derivedFrom":sQuery(id+"F48.wireOp",EDGE,"E132")}),-1.0]])]});
            var Q1;
            Q1=makeQuery(id+"F26.opExtrude","CAP_FACE",FACE,{"disambiguationData":[OSD([sQuery(id+"F25.wireOp",EDGE,"E51"),sQuery(id+"F25.wireOp",EDGE,"E52"),sQuery(id+"F25.wireOp",EDGE,"E53"),sQuery(id+"F25.wireOp",EDGE,"E54"),sQuery(id+"F25.wireOp",EDGE,"E55"),sQuery(id+"F25.wireOp",EDGE,"E56"),sQuery(id+"F25.wireOp",EDGE,"E57"),sQuery(id+"F25.wireOp",EDGE,"E58"),sQuery(id+"F25.wireOp",EDGE,"E59"),sQuery(id+"F25.wireOp",EDGE,"E60")])],"isStart":true});
            extrude(context, id + "F49", {"entities" : qUnion([Q0]), "operationType" : NewBodyOperationType.ADD, "endBound" : BoundingType.UP_TO_SURFACE, "oppositeDirection" : true, "depth" : 25 * mm, "endBoundEntityFace" : qUnion([Q1]), "offsetDistance" : 25 * mm});
        }
        {
            var Q0;
            Q0=makeQuery(id+"F45.opPattern","COPY",BODY,{"derivedFrom":makeQuery(id+"F44.opExtrude","SWEPT_BODY",BODY,{"disambiguationData":[OSD([sQuery(id+"F43.wireOp",EDGE,"E115"),sQuery(id+"F43.wireOp",EDGE,"E116"),sQuery(id+"F43.wireOp",EDGE,"E117"),sQuery(id+"F43.wireOp",EDGE,"E118"),sQuery(id+"F43.wireOp",EDGE,"E119"),sQuery(id+"F43.wireOp",EDGE,"E120"),sQuery(id+"F43.wireOp",EDGE,"E121"),sQuery(id+"F43.wireOp",EDGE,"E122")])]}),"instanceName":"1"});
            transform(context, id + "F50", {"entities" : qUnion([Q0]), "transformType" : TransformType.TRANSLATION_3D, "dx" : 5 * mm, "dy" : 0 * mm, "dz" : 0 * mm, "makeCopy" : false});
        }
        {
            var Q0;
            Q0=sQuery(id+"F11.wireOp",VERTEX,"E21.start");
            var Q1;
            Q1=sQuery(id+"F11.wireOp",EDGE,"E20");
            cPlane(context, id + "F51", {"entities" : qUnion([Q0, Q1]), "cplaneType" : CPlaneType.LINE_POINT, "offset" : 25 * mm, "width" : 150 * mm, "height" : 150 * mm});
        }
        {
            var Q0;
            {var subQ3=sQuery(id+"F23.wireOp",EDGE,"E46.0");Q0=makeQuery(id+"F23.imprint","IMPRINT",FACE,{"disambiguationData":[TD([[makeQuery(id+"F23.imprint","IMPRINT",EDGE,{"derivedFrom":subQ3}),1.0]])]});}
            extrude(context, id + "F52", {"entities" : qUnion([Q0]), "operationType" : NewBodyOperationType.REMOVE, "oppositeDirection" : true, "depth" : 5 * mm, "offsetDistance" : 25 * mm});
        }
    });
